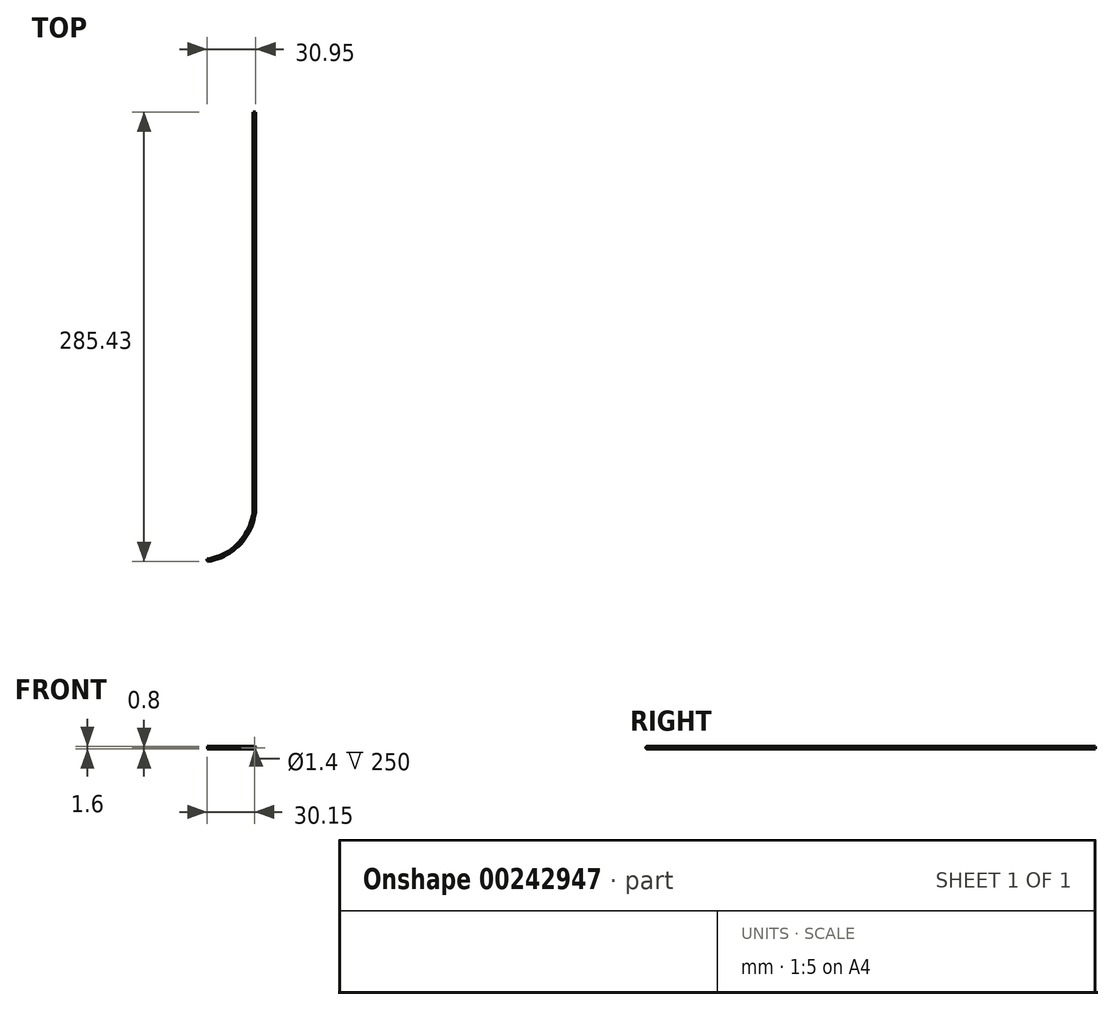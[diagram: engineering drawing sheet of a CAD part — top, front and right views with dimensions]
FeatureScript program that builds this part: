
annotation { "Feature Type Name" : "Feature", "Feature Type Description" : "" }
export const myFeature = defineFeature(function(context is Context, id is Id, definition is map)
    precondition{}
    {
        {
            var Q0;
            Q0=qCreatedBy(makeId("Front.planeOp"),FACE);
            var sketch = newSketch(context, id + "F0", { "sketchPlane" : qUnion([Q0])});
            skCircle(sketch, "E0", {"center": v(0, 0) * mm, "radius": 0.7 * mm});
            skCircle(sketch, "E1", {"center": v(0, 0) * mm, "radius": 0.8 * mm});
            skSolve(sketch);
        }
        {
            var Q0;
            Q0=qCreatedBy(makeId("Top.planeOp"),FACE);
            var sketch = newSketch(context, id + "F1", { "sketchPlane" : qUnion([Q0])});
            skLineSegment(sketch, "E2", {"start": v(0, 0) * mm, "end": v(0, -250) * mm});
            skLineSegment(sketch, "E3", {"start": v(0, -145.32) * mm, "end": v(0, -250) * mm, "construction": true});
            skLineSegment(sketch, "E4", {"start": v(0, -250) * mm, "end": v(-35, -250) * mm, "construction": true});
            skArc(sketch, "E5", {"start": v(0, -250) * mm, "mid": v(-8.56, -272.93) * mm, "end": v(-30.04, -284.65) * mm});
            skSolve(sketch);
        }
        {
            var Q0;
            Q0=makeQuery(id+"F0.imprint","IMPRINT",FACE,{"disambiguationData":[TD([[makeQuery(id+"F0.imprint","IMPRINT",EDGE,{"derivedFrom":sQuery(id+"F0.wireOp",EDGE,"E0")}),-1.0]])]});
            var Q1;
            Q1=sQuery(id+"F1.wireOp",EDGE,"E2");
            var Q2;
            Q2=sQuery(id+"F1.wireOp",EDGE,"E5");
            sweep(context, id + "F2", {"profiles" : qUnion([Q0]), "path" : qUnion([Q1, Q2])});
        }
    });
